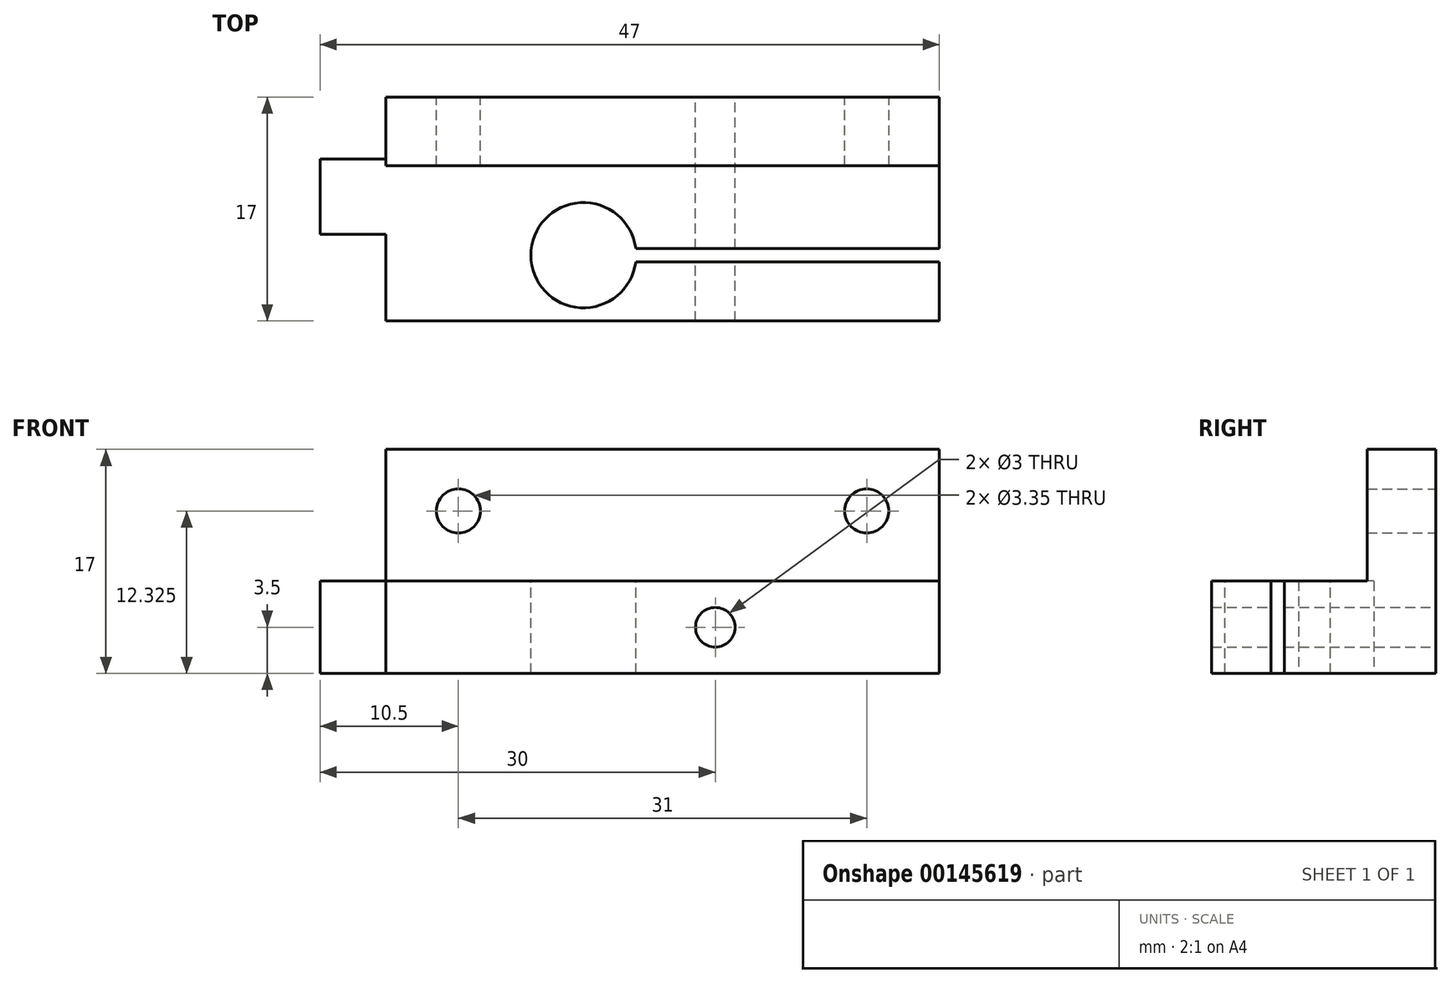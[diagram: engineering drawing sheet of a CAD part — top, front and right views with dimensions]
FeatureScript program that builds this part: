
annotation { "Feature Type Name" : "Feature", "Feature Type Description" : "" }
export const myFeature = defineFeature(function(context is Context, id is Id, definition is map)
    precondition{}
    {
        {
            var Q0;
            Q0=qCreatedBy(makeId("Top.planeOp"),FACE);
            var sketch = newSketch(context, id + "F0", { "sketchPlane" : qUnion([Q0])});
            skLineSegment(sketch, "E0.bottom", {"start": v(0, 0) * mm, "end": v(42, 0) * mm});
            skLineSegment(sketch, "E0.top", {"start": v(0, 17) * mm, "end": v(42, 17) * mm});
            skLineSegment(sketch, "E0.left", {"start": v(0, 0) * mm, "end": v(0, 17) * mm});
            skLineSegment(sketch, "E0.right", {"start": v(42, 0) * mm, "end": v(42, 17) * mm});
            skSolve(sketch);
        }
        {
            var Q0;
            Q0=qSketchRegion(id+"F0",true);
            extrude(context, id + "F1", {"entities" : qUnion([Q0]), "depth" : 7 * mm});
        }
        {
            var Q0;
            Q0=makeQuery(id+"F1.opExtrude","CAP_FACE",FACE,{"disambiguationData":[OSD([sQuery(id+"F0.wireOp",EDGE,"E0.bottom"),sQuery(id+"F0.wireOp",EDGE,"E0.top"),sQuery(id+"F0.wireOp",EDGE,"E0.left"),sQuery(id+"F0.wireOp",EDGE,"E0.right")])],"isStart":false});
            var sketch = newSketch(context, id + "F2", { "sketchPlane" : qUnion([Q0])});
            skCircle(sketch, "E1", {"center": v(15, 5) * mm, "radius": 4 * mm});
            skLineSegment(sketch, "E2", {"start": v(15, 5) * mm, "end": v(42, 5) * mm});
            skLineSegment(sketch, "E3", {"start": v(42, 5) * mm, "end": v(42, 4.5) * mm});
            skLineSegment(sketch, "E4", {"start": v(42, 4.5) * mm, "end": v(18.97, 4.5) * mm});
            skLineSegment(sketch, "E5", {"start": v(42, 5) * mm, "end": v(42, 5.5) * mm});
            skLineSegment(sketch, "E6", {"start": v(42, 5.5) * mm, "end": v(18.97, 5.5) * mm});
            skSolve(sketch);
        }
        {
            var Q0;
            Q0=makeQuery(id+"F1.opExtrude","SWEPT_FACE",FACE,{"disambiguationData":[OSD([sQuery(id+"F0.wireOp",EDGE,"E0.top")])]});
            var sketch = newSketch(context, id + "F3", { "sketchPlane" : qUnion([Q0])});
            skCircle(sketch, "E7", {"center": v(-25, 3.5) * mm, "radius": 1.5 * mm});
            skLineSegment(sketch, "E8", {"start": v(-25, 3.5) * mm, "end": v(-42, 3.5) * mm});
            skSolve(sketch);
        }
        {
            var Q0;
            Q0=qSketchRegion(id+"F3",true);
            extrude(context, id + "F4", {"entities" : qUnion([Q0]), "operationType" : NewBodyOperationType.REMOVE, "oppositeDirection" : true, "depth" : 25 * mm});
        }
        {
            var Q0;
            Q0=makeQuery(id+"F1.opExtrude","CAP_FACE",FACE,{"disambiguationData":[OSD([sQuery(id+"F0.wireOp",EDGE,"E0.bottom"),sQuery(id+"F0.wireOp",EDGE,"E0.top"),sQuery(id+"F0.wireOp",EDGE,"E0.left"),sQuery(id+"F0.wireOp",EDGE,"E0.right")])],"isStart":false});
            var sketch = newSketch(context, id + "F5", { "sketchPlane" : qUnion([Q0])});
            skLineSegment(sketch, "E9.bottom", {"start": v(0, 17) * mm, "end": v(42, 17) * mm});
            skLineSegment(sketch, "E9.top", {"start": v(0, 11.8) * mm, "end": v(42, 11.8) * mm});
            skLineSegment(sketch, "E9.left", {"start": v(0, 17) * mm, "end": v(0, 11.8) * mm});
            skLineSegment(sketch, "E9.right", {"start": v(42, 17) * mm, "end": v(42, 11.8) * mm});
            skSolve(sketch);
        }
        {
            var Q0;
            Q0=makeQuery(id+"F5.imprint","IMPRINT",FACE,{"disambiguationData":[TD([[makeQuery(id+"F5.imprint","IMPRINT",EDGE,{"derivedFrom":sQuery(id+"F5.wireOp",EDGE,"E9.bottom")}),-1.0]])]});
            extrude(context, id + "F6", {"entities" : qUnion([Q0]), "operationType" : NewBodyOperationType.ADD, "depth" : 10 * mm});
        }
        {
            var Q0;
            Q0=makeQuery(id+"F6.boolean.opBoolean","MERGE",FACE,{"derivedFrom":[makeQuery(id+"F1.opExtrude","SWEPT_FACE",FACE,{"disambiguationData":[OSD([sQuery(id+"F0.wireOp",EDGE,"E0.top")])]}),makeQuery(id+"F6.opExtrude","SWEPT_FACE",FACE,{"disambiguationData":[OSD([sQuery(id+"FFFDCbTcivKPk1C_1.wireOp",EDGE,"d29ae964-e38a-46b3-8ff4-cadffaec6662.bottom")])]})]});
            var sketch = newSketch(context, id + "F7", { "sketchPlane" : qUnion([Q0])});
            skCircle(sketch, "E10", {"center": v(-36.5, 12.33) * mm, "radius": 1.68 * mm});
            skCircle(sketch, "E11", {"center": v(-5.5, 12.33) * mm, "radius": 1.68 * mm});
            skSolve(sketch);
        }
        {
            var Q0;
            Q0=qSketchRegion(id+"F7",true);
            extrude(context, id + "F8", {"entities" : qUnion([Q0]), "operationType" : NewBodyOperationType.REMOVE, "oppositeDirection" : true, "depth" : 25 * mm});
        }
        {
            var Q0;
            Q0=qSketchRegion(id+"F2",true);
            extrude(context, id + "F9", {"entities" : qUnion([Q0]), "operationType" : NewBodyOperationType.REMOVE, "oppositeDirection" : true, "depth" : 25 * mm});
        }
        {
            var Q0;
            Q0=makeQuery(id+"F6.boolean.opBoolean","MERGE",FACE,{"derivedFrom":[makeQuery(id+"F1.opExtrude","SWEPT_FACE",FACE,{"disambiguationData":[OSD([sQuery(id+"F0.wireOp",EDGE,"E0.left")])]}),makeQuery(id+"F6.opExtrude","SWEPT_FACE",FACE,{"disambiguationData":[OSD([sQuery(id+"F5.wireOp",EDGE,"E9.left")])]})]});
            var sketch = newSketch(context, id + "F10", { "sketchPlane" : qUnion([Q0])});
            skLineSegment(sketch, "E12.bottom", {"start": v(-12.3, 7) * mm, "end": v(-6.6, 7) * mm});
            skLineSegment(sketch, "E12.top", {"start": v(-12.3, 0) * mm, "end": v(-6.6, 0) * mm});
            skLineSegment(sketch, "E12.left", {"start": v(-12.3, 7) * mm, "end": v(-12.3, 0) * mm});
            skLineSegment(sketch, "E12.right", {"start": v(-6.6, 7) * mm, "end": v(-6.6, 0) * mm});
            skSolve(sketch);
        }
        {
            var Q0;
            Q0=qSketchRegion(id+"F10",true);
            extrude(context, id + "F11", {"entities" : qUnion([Q0]), "operationType" : NewBodyOperationType.ADD, "depth" : 5 * mm});
        }
    });
